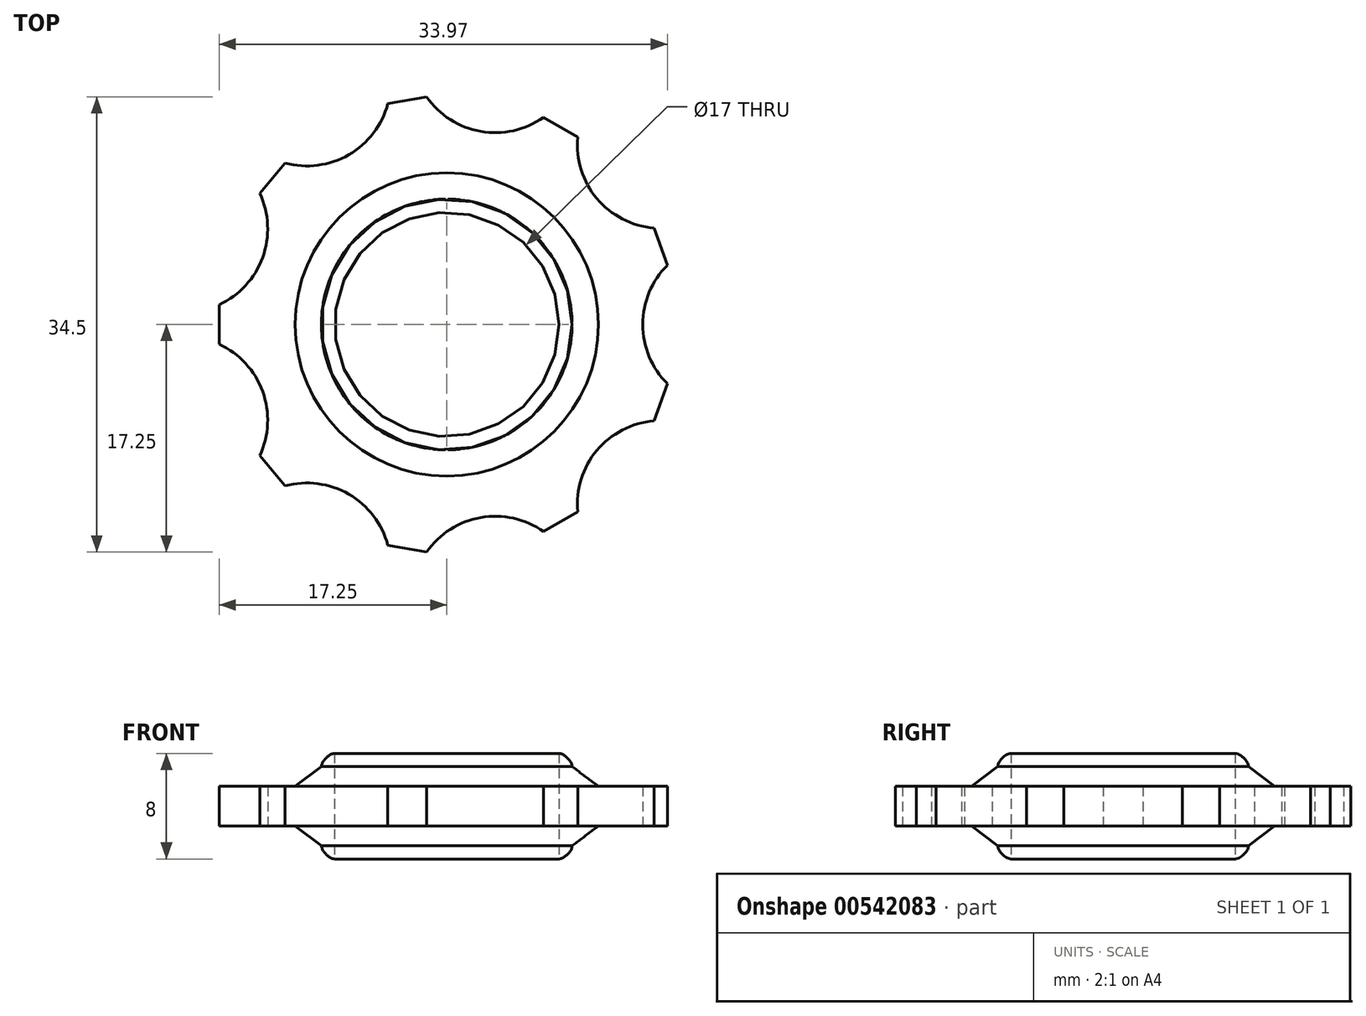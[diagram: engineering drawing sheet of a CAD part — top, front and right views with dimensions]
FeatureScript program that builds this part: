
annotation { "Feature Type Name" : "Feature", "Feature Type Description" : "" }
export const myFeature = defineFeature(function(context is Context, id is Id, definition is map)
    precondition{}
    {
        {
            var Q0;
            Q0=qCreatedBy(makeId("Top.planeOp"),FACE);
            var sketch = newSketch(context, id + "F0", { "sketchPlane" : qUnion([Q0])});
            skCircle(sketch, "E0.cCircle", {"center": v(0, 0) * mm, "radius": 14.85 * mm, "construction": true});
            skLineSegment(sketch, "E0.0", {"start": v(14.85, 5.4) * mm, "end": v(14.85, -5.4) * mm, "construction": true});
            skLineSegment(sketch, "E0.1", {"start": v(14.85, -5.4) * mm, "end": v(7.9, -13.69) * mm, "construction": true});
            skLineSegment(sketch, "E0.2", {"start": v(7.9, -13.69) * mm, "end": v(-2.74, -15.56) * mm, "construction": true});
            skLineSegment(sketch, "E0.3", {"start": v(-2.74, -15.56) * mm, "end": v(-12.1, -10.16) * mm, "construction": true});
            skLineSegment(sketch, "E0.4", {"start": v(-12.1, -10.16) * mm, "end": v(-15.8, 0) * mm, "construction": true});
            skLineSegment(sketch, "E0.5", {"start": v(-15.8, 0) * mm, "end": v(-12.1, 10.16) * mm, "construction": true});
            skLineSegment(sketch, "E0.6", {"start": v(-12.1, 10.16) * mm, "end": v(-2.74, 15.56) * mm, "construction": true});
            skLineSegment(sketch, "E0.7", {"start": v(-2.74, 15.56) * mm, "end": v(7.9, 13.69) * mm, "construction": true});
            skLineSegment(sketch, "E0.8", {"start": v(7.9, 13.69) * mm, "end": v(14.85, 5.4) * mm, "construction": true});
            skPoint(sketch, "E0.0.midPoint", {"position": v(14.85, 0) * mm});
            skLineSegment(sketch, "E1.0", {"start": v(14.85, 0) * mm, "end": v(11.38, -9.55) * mm, "construction": true});
            skLineSegment(sketch, "E1.1", {"start": v(11.38, -9.55) * mm, "end": v(2.58, -14.62) * mm, "construction": true});
            skLineSegment(sketch, "E1.2", {"start": v(2.58, -14.62) * mm, "end": v(-7.43, -12.86) * mm, "construction": true});
            skLineSegment(sketch, "E1.3", {"start": v(-7.42, -12.86) * mm, "end": v(-13.95, -5.08) * mm, "construction": true});
            skLineSegment(sketch, "E1.4", {"start": v(-13.95, -5.08) * mm, "end": v(-13.95, 5.08) * mm, "construction": true});
            skLineSegment(sketch, "E1.5", {"start": v(-13.95, 5.08) * mm, "end": v(-7.43, 12.86) * mm, "construction": true});
            skLineSegment(sketch, "E1.6", {"start": v(-7.43, 12.86) * mm, "end": v(2.58, 14.62) * mm, "construction": true});
            skLineSegment(sketch, "E1.7", {"start": v(2.58, 14.62) * mm, "end": v(11.38, 9.55) * mm, "construction": true});
            skLineSegment(sketch, "E1.8", {"start": v(11.38, 9.55) * mm, "end": v(14.85, 0) * mm, "construction": true});
            skCircle(sketch, "E2.cCircle", {"center": v(0, 0) * mm, "radius": 17.25 * mm, "construction": true});
            skLineSegment(sketch, "E2.0", {"start": v(-17.25, 0) * mm, "end": v(-13.21, 11.09) * mm, "construction": true});
            skLineSegment(sketch, "E2.1", {"start": v(-13.21, 11.09) * mm, "end": v(-3, 16.99) * mm, "construction": true});
            skLineSegment(sketch, "E2.2", {"start": v(-3, 16.99) * mm, "end": v(8.62, 14.94) * mm, "construction": true});
            skLineSegment(sketch, "E2.3", {"start": v(8.62, 14.94) * mm, "end": v(16.2, 5.9) * mm, "construction": true});
            skLineSegment(sketch, "E2.4", {"start": v(16.2, 5.9) * mm, "end": v(16.2, -5.9) * mm, "construction": true});
            skLineSegment(sketch, "E2.5", {"start": v(16.2, -5.9) * mm, "end": v(8.63, -14.94) * mm, "construction": true});
            skLineSegment(sketch, "E2.6", {"start": v(8.63, -14.94) * mm, "end": v(-3, -16.99) * mm, "construction": true});
            skLineSegment(sketch, "E2.7", {"start": v(-3, -16.99) * mm, "end": v(-13.21, -11.09) * mm, "construction": true});
            skLineSegment(sketch, "E2.8", {"start": v(-13.21, -11.09) * mm, "end": v(-17.25, 0) * mm, "construction": true});
            skLineSegment(sketch, "E3", {"start": v(-13.21, 11.09) * mm, "end": v(-12.25, 12.24) * mm});
            skLineSegment(sketch, "E4", {"start": v(-13.21, 11.09) * mm, "end": v(-14.18, 9.94) * mm});
            skLineSegment(sketch, "E5", {"start": v(-3, 16.99) * mm, "end": v(-1.52, 17.25) * mm});
            skLineSegment(sketch, "E6", {"start": v(-3, 16.99) * mm, "end": v(-4.47, 16.73) * mm});
            skLineSegment(sketch, "E7", {"start": v(8.62, 14.94) * mm, "end": v(9.92, 14.19) * mm});
            skLineSegment(sketch, "E8", {"start": v(8.62, 14.94) * mm, "end": v(7.33, 15.69) * mm});
            skLineSegment(sketch, "E9", {"start": v(16.2, 5.9) * mm, "end": v(15.7, 7.3) * mm});
            skLineSegment(sketch, "E10", {"start": v(16.2, 5.9) * mm, "end": v(16.72, 4.5) * mm});
            skLineSegment(sketch, "E11", {"start": v(16.2, -5.9) * mm, "end": v(16.72, -4.5) * mm});
            skLineSegment(sketch, "E12", {"start": v(16.2, -5.9) * mm, "end": v(15.7, -7.3) * mm});
            skLineSegment(sketch, "E13", {"start": v(8.63, -14.94) * mm, "end": v(9.92, -14.19) * mm});
            skLineSegment(sketch, "E14", {"start": v(8.63, -14.94) * mm, "end": v(7.33, -15.69) * mm});
            skLineSegment(sketch, "E15", {"start": v(-3, -16.99) * mm, "end": v(-1.52, -17.25) * mm});
            skLineSegment(sketch, "E16", {"start": v(-3, -16.99) * mm, "end": v(-4.47, -16.73) * mm});
            skLineSegment(sketch, "E17", {"start": v(-13.21, -11.09) * mm, "end": v(-12.25, -12.24) * mm});
            skLineSegment(sketch, "E18", {"start": v(-13.21, -11.09) * mm, "end": v(-14.18, -9.94) * mm});
            skLineSegment(sketch, "E19", {"start": v(-17.25, 0) * mm, "end": v(-17.25, -1.5) * mm});
            skLineSegment(sketch, "E20", {"start": v(-17.25, 0) * mm, "end": v(-17.25, 1.5) * mm});
            skArc(sketch, "E21", {"start": v(-1.52, 17.25) * mm, "mid": v(2.58, 14.62) * mm, "end": v(7.33, 15.69) * mm});
            skArc(sketch, "E22", {"start": v(9.92, 14.19) * mm, "mid": v(11.38, 9.55) * mm, "end": v(15.7, 7.3) * mm});
            skArc(sketch, "E23", {"start": v(15.7, -7.3) * mm, "mid": v(11.38, -9.55) * mm, "end": v(9.92, -14.19) * mm});
            skArc(sketch, "E24", {"start": v(7.33, -15.69) * mm, "mid": v(2.58, -14.62) * mm, "end": v(-1.52, -17.25) * mm});
            skArc(sketch, "E25", {"start": v(-4.47, -16.73) * mm, "mid": v(-7.42, -12.86) * mm, "end": v(-12.25, -12.24) * mm});
            skArc(sketch, "E26", {"start": v(-14.18, -9.94) * mm, "mid": v(-13.95, -5.08) * mm, "end": v(-17.25, -1.5) * mm});
            skArc(sketch, "E27", {"start": v(-17.25, 1.5) * mm, "mid": v(-13.95, 5.08) * mm, "end": v(-14.18, 9.94) * mm});
            skArc(sketch, "E28", {"start": v(-12.25, 12.24) * mm, "mid": v(-7.43, 12.86) * mm, "end": v(-4.47, 16.73) * mm});
            skArc(sketch, "E29", {"start": v(16.72, 4.5) * mm, "mid": v(14.85, 0) * mm, "end": v(16.72, -4.5) * mm});
            skCircle(sketch, "E30", {"center": v(0, 0) * mm, "radius": 8.5 * mm});
            skCircle(sketch, "E31", {"center": v(0, 0) * mm, "radius": 9.5 * mm});
            skCircle(sketch, "E32", {"center": v(0, 0) * mm, "radius": 11.5 * mm});
            skSolve(sketch);
        }
        {
            var Q0;
            Q0=makeQuery(id+"F0.imprint","IMPRINT",FACE,{"disambiguationData":[TD([[makeQuery(id+"F0.imprint","IMPRINT",EDGE,{"derivedFrom":sQuery(id+"F0.wireOp",EDGE,"E3")}),-1.0]])]});
            extrude(context, id + "F1", {"entities" : qUnion([Q0]), "depth" : 1.5 * mm, "offsetDistance" : 25 * mm});
        }
        {
            var Q0;
            Q0=makeQuery(id+"F0.imprint","IMPRINT",FACE,{"disambiguationData":[TD([[makeQuery(id+"F0.imprint","IMPRINT",EDGE,{"derivedFrom":sQuery(id+"F0.wireOp",EDGE,"E31")}),-1.0]])]});
            extrude(context, id + "F2", {"entities" : qUnion([Q0]), "operationType" : NewBodyOperationType.ADD, "depth" : 3 * mm, "offsetDistance" : 25 * mm});
        }
        {
            var Q0;
            Q0=makeQuery(id+"F0.imprint","IMPRINT",FACE,{"disambiguationData":[TD([[makeQuery(id+"F0.imprint","IMPRINT",EDGE,{"derivedFrom":sQuery(id+"F0.wireOp",EDGE,"E30")}),-1.0]])]});
            extrude(context, id + "F3", {"entities" : qUnion([Q0]), "operationType" : NewBodyOperationType.ADD, "depth" : 4 * mm, "offsetDistance" : 25 * mm});
        }
        {
            var Q0;
            Q0=makeQuery(id+"F2.opExtrude","CAP_EDGE",EDGE,{"disambiguationData":[OSD([sQuery(id+"F0.wireOp",EDGE,"E32")])],"isStart":false});
            chamfer(context, id + "F4", {"entities" : qUnion([Q0]), "chamferType" : ChamferType.OFFSET_ANGLE, "width" : 2 * mm, "oppositeDirection" : false, "angle" : 37 * degree, "tangentPropagation" : true});
        }
        {
            var Q0;
            Q0=makeQuery(id+"F3.opExtrude","CAP_EDGE",EDGE,{"disambiguationData":[OSD([sQuery(id+"F0.wireOp",EDGE,"E31")])],"isStart":false});
            fillet(context, id + "F5", {"entities" : qUnion([Q0]), "radius" : 1 * mm, "tangentPropagation" : true, "rho" : 0.3, "crossSection" : FilletCrossSection.CONIC, "allowEdgeOverflow" : false});
        }
        {
            var Q0;
            Q0=makeQuery(id+"F1.opExtrude","SWEPT_BODY",BODY,{"disambiguationData":[OSD([sQuery(id+"F0.wireOp",EDGE,"E3"),sQuery(id+"F0.wireOp",EDGE,"E4"),sQuery(id+"F0.wireOp",EDGE,"E5"),sQuery(id+"F0.wireOp",EDGE,"E6"),sQuery(id+"F0.wireOp",EDGE,"E7"),sQuery(id+"F0.wireOp",EDGE,"E8"),sQuery(id+"F0.wireOp",EDGE,"E9"),sQuery(id+"F0.wireOp",EDGE,"E10"),sQuery(id+"F0.wireOp",EDGE,"E11"),sQuery(id+"F0.wireOp",EDGE,"E12"),sQuery(id+"F0.wireOp",EDGE,"E13"),sQuery(id+"F0.wireOp",EDGE,"E14"),sQuery(id+"F0.wireOp",EDGE,"E15"),sQuery(id+"F0.wireOp",EDGE,"E16"),sQuery(id+"F0.wireOp",EDGE,"E17"),sQuery(id+"F0.wireOp",EDGE,"E18"),sQuery(id+"F0.wireOp",EDGE,"E19"),sQuery(id+"F0.wireOp",EDGE,"E20"),sQuery(id+"F0.wireOp",EDGE,"E21"),sQuery(id+"F0.wireOp",EDGE,"E22"),sQuery(id+"F0.wireOp",EDGE,"E23"),sQuery(id+"F0.wireOp",EDGE,"E24"),sQuery(id+"F0.wireOp",EDGE,"E25"),sQuery(id+"F0.wireOp",EDGE,"E26"),sQuery(id+"F0.wireOp",EDGE,"E27"),sQuery(id+"F0.wireOp",EDGE,"E28"),sQuery(id+"F0.wireOp",EDGE,"E29"),sQuery(id+"F0.wireOp",EDGE,"E32")])]});
            var Q1;
            {var subQ0=sQuery(id+"F0.wireOp",EDGE,"E31");var subQ1=sQuery(id+"F0.wireOp",EDGE,"E32");Q1=makeQuery(id+"F3.boolean.opBoolean","MERGE",FACE,{"derivedFrom":[makeQuery(id+"F2.boolean.opBoolean","MERGE",FACE,{"derivedFrom":[makeQuery(id+"F1.opExtrude","CAP_FACE",FACE,{"disambiguationData":[OSD([sQuery(id+"F0.wireOp",EDGE,"E3"),sQuery(id+"F0.wireOp",EDGE,"E4"),sQuery(id+"F0.wireOp",EDGE,"E5"),sQuery(id+"F0.wireOp",EDGE,"E6"),sQuery(id+"F0.wireOp",EDGE,"E7"),sQuery(id+"F0.wireOp",EDGE,"E8"),sQuery(id+"F0.wireOp",EDGE,"E9"),sQuery(id+"F0.wireOp",EDGE,"E10"),sQuery(id+"F0.wireOp",EDGE,"E11"),sQuery(id+"F0.wireOp",EDGE,"E12"),sQuery(id+"F0.wireOp",EDGE,"E13"),sQuery(id+"F0.wireOp",EDGE,"E14"),sQuery(id+"F0.wireOp",EDGE,"E15"),sQuery(id+"F0.wireOp",EDGE,"E16"),sQuery(id+"F0.wireOp",EDGE,"E17"),sQuery(id+"F0.wireOp",EDGE,"E18"),sQuery(id+"F0.wireOp",EDGE,"E19"),sQuery(id+"F0.wireOp",EDGE,"E20"),sQuery(id+"F0.wireOp",EDGE,"E21"),sQuery(id+"F0.wireOp",EDGE,"E22"),sQuery(id+"F0.wireOp",EDGE,"E23"),sQuery(id+"F0.wireOp",EDGE,"E24"),sQuery(id+"F0.wireOp",EDGE,"E25"),sQuery(id+"F0.wireOp",EDGE,"E26"),sQuery(id+"F0.wireOp",EDGE,"E27"),sQuery(id+"F0.wireOp",EDGE,"E28"),sQuery(id+"F0.wireOp",EDGE,"E29"),subQ1])],"isStart":true}),makeQuery(id+"F2.opExtrude","CAP_FACE",FACE,{"disambiguationData":[OSD([subQ0,subQ1])],"isStart":true})]}),makeQuery(id+"F3.opExtrude","CAP_FACE",FACE,{"disambiguationData":[OSD([sQuery(id+"F0.wireOp",EDGE,"E30"),subQ0])],"isStart":true})]});}
            mirror(context, id + "F6", {"operationType" : NewBodyOperationType.ADD, "entities" : qUnion([Q0]), "mirrorPlane" : qUnion([Q1])});
        }
    });
